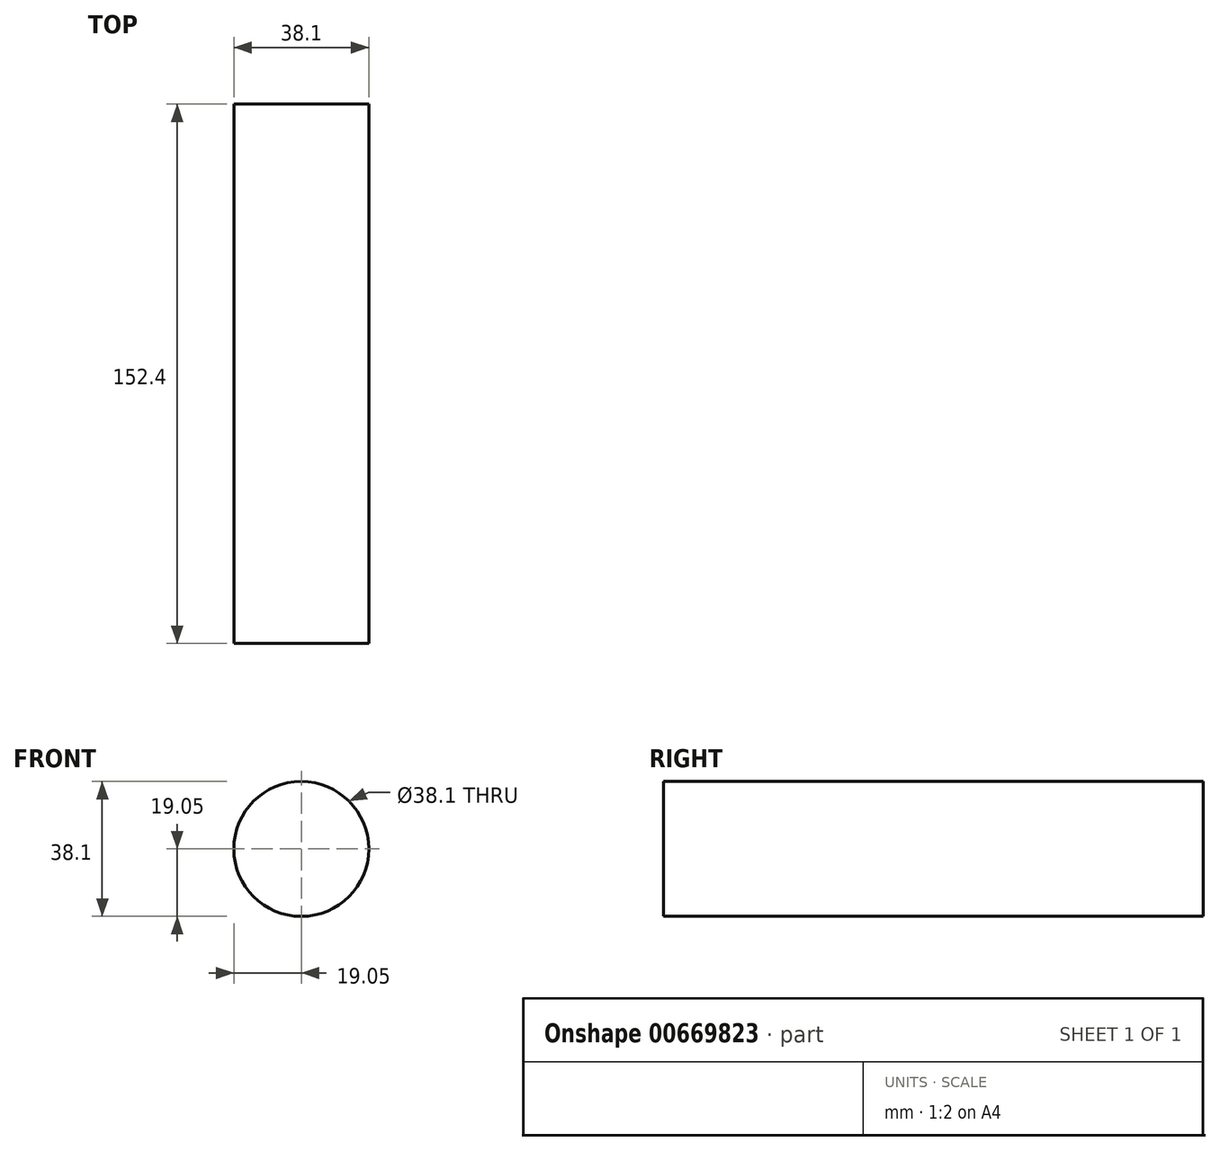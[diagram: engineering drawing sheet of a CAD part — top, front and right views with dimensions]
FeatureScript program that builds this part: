
annotation { "Feature Type Name" : "Feature", "Feature Type Description" : "" }
export const myFeature = defineFeature(function(context is Context, id is Id, definition is map)
    precondition{}
    {
        {
            var Q0;
            Q0=qCreatedBy(makeId("Front.planeOp"),FACE);
            var sketch = newSketch(context, id + "F0", { "sketchPlane" : qUnion([Q0])});
            skCircle(sketch, "E0", {"center": v(0, 0) * mm, "radius": 19.05 * mm});
            skArc(sketch, "E1", {"start": v(2.63, -18.87) * mm, "mid": v(23.05, -29.9) * mm, "end": v(17.58, -7.35) * mm});
            skArc(sketch, "E2", {"start": v(-16.77, -9.03) * mm, "mid": v(-15.87, -31.16) * mm, "end": v(2.56, -18.88) * mm});
            skSolve(sketch);
        }
        {
            var Q0;
            Q0=sQuery(id+"F0.wireOp",EDGE,"E0");
            extrude(context, id + "F1", {"bodyType" : ToolBodyType.SURFACE, "surfaceEntities" : qUnion([Q0]), "oppositeDirection" : true, "depth" : 152.4 * mm, "offsetDistance" : 25.4 * mm});
        }
    });
